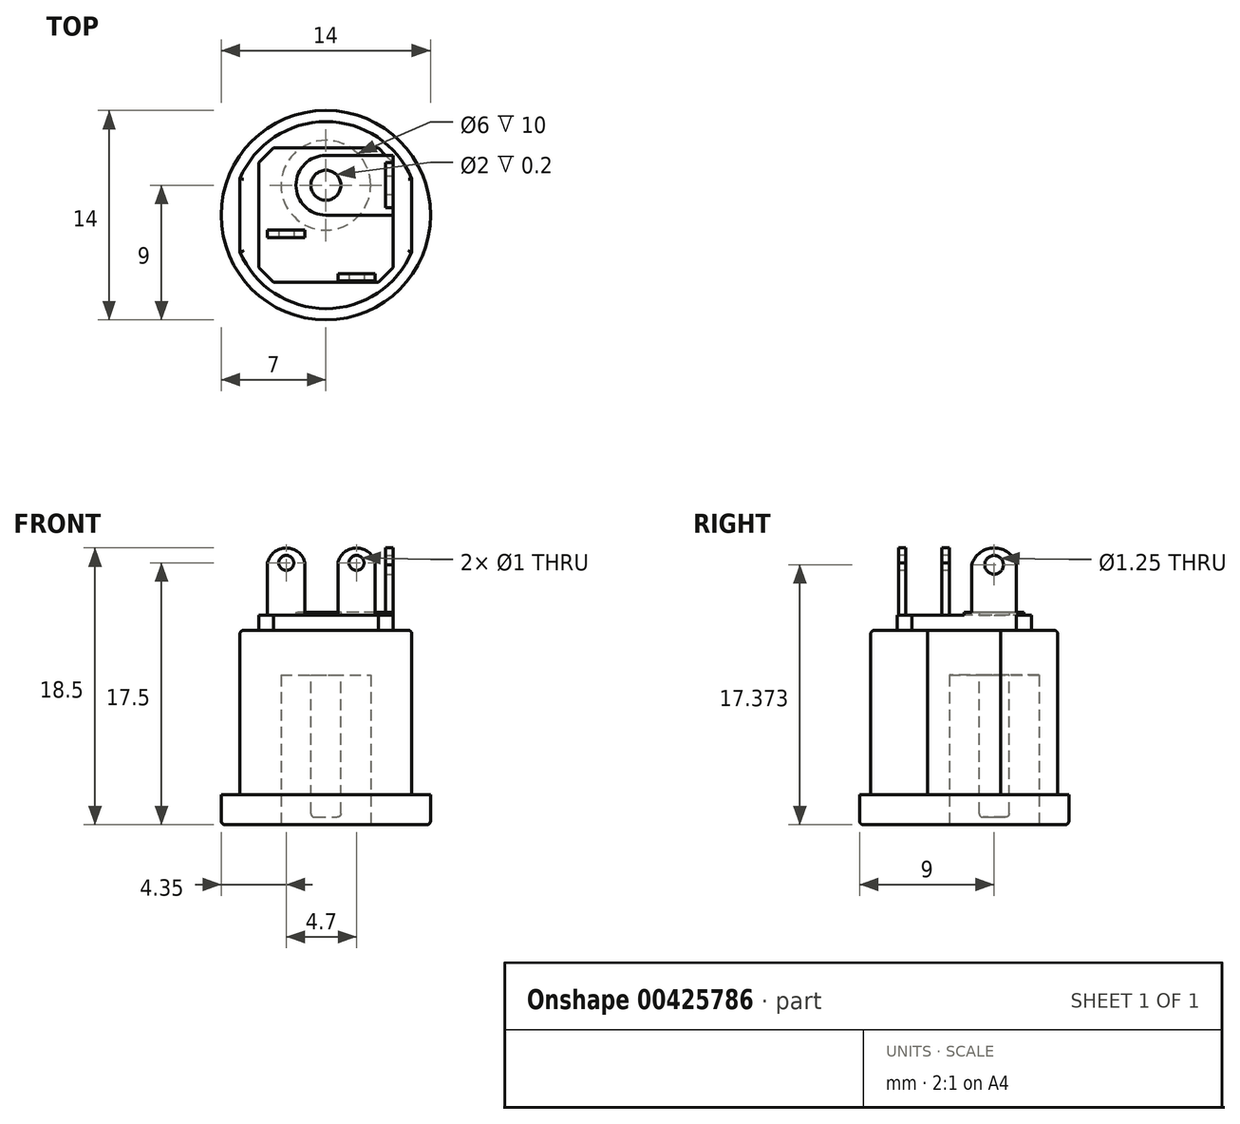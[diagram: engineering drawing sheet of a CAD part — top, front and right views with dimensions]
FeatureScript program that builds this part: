
annotation { "Feature Type Name" : "Feature", "Feature Type Description" : "" }
export const myFeature = defineFeature(function(context is Context, id is Id, definition is map)
    precondition{}
    {
        {
            var Q0;
            Q0=qCreatedBy(makeId("Top.planeOp"),FACE);
            var sketch = newSketch(context, id + "F0", { "sketchPlane" : qUnion([Q0])});
            skCircle(sketch, "E0", {"center": v(0, 0) * mm, "radius": 7 * mm});
            skSolve(sketch);
        }
        {
            var Q0;
            Q0 = qSketchRegion(id + "F0", true);
            extrude(context, id + "F1", {"entities" : qUnion([Q0]), "depth" : 2 * mm});
        }
        {
            var Q0;
            Q0=makeQuery(id+"F1.opExtrude","CAP_FACE",FACE,{"disambiguationData":[OSD([sQuery(id+"F0.wireOp",EDGE,"E0")])],"isStart":false});
            var sketch = newSketch(context, id + "F2", { "sketchPlane" : qUnion([Q0])});
            skArc(sketch, "E1", {"start": v(-5.75, -2.45) * mm, "mid": v(0, -6.25) * mm, "end": v(5.75, -2.45) * mm});
            skLineSegment(sketch, "E2", {"start": v(5.75, 2.45) * mm, "end": v(5.75, -2.45) * mm});
            skLineSegment(sketch, "E3", {"start": v(0, 8.24) * mm, "end": v(0, -10) * mm, "construction": true});
            skLineSegment(sketch, "E4.MirrorCS", {"start": v(-5.75, 2.45) * mm, "end": v(-5.75, -2.45) * mm});
            skPoint(sketch, "E5.orphan", {"position": v(-5.75, 5.82) * mm});
            skPoint(sketch, "E6.orphan", {"position": v(-5.75, -6.76) * mm});
            skPoint(sketch, "E7.orphan", {"position": v(5.75, 5.82) * mm});
            skArc(sketch, "E8.trimOffspring", {"start": v(5.75, 2.45) * mm, "mid": v(0, 6.25) * mm, "end": v(-5.75, 2.45) * mm});
            skPoint(sketch, "E9.orphan", {"position": v(5.75, -6.76) * mm});
            skSolve(sketch);
        }
        {
            var Q0;
            Q0 = qSketchRegion(id + "F2", true);
            extrude(context, id + "F3", {"entities" : qUnion([Q0]), "operationType" : NewBodyOperationType.ADD, "depth" : 11 * mm});
        }
        {
            var Q0;
            Q0=makeQuery(id+"F1.opExtrude","CAP_FACE",FACE,{"disambiguationData":[OSD([sQuery(id+"F0.wireOp",EDGE,"E0")])],"isStart":true});
            var sketch = newSketch(context, id + "F4", { "sketchPlane" : qUnion([Q0])});
            skCircle(sketch, "E10", {"center": v(0, -2) * mm, "radius": 3 * mm});
            skSolve(sketch);
        }
        {
            var Q0;
            Q0 = qSketchRegion(id + "F4", true);
            extrude(context, id + "F5", {"entities" : qUnion([Q0]), "operationType" : NewBodyOperationType.REMOVE, "oppositeDirection" : true, "depth" : 10 * mm});
        }
        {
            var Q0;
            Q0=makeQuery(id+"F3.opExtrude","CAP_FACE",FACE,{"disambiguationData":[OSD([sQuery(id+"F2.wireOp",EDGE,"E1"),sQuery(id+"F2.wireOp",EDGE,"E2"),sQuery(id+"F2.wireOp",EDGE,"E4.MirrorCS"),sQuery(id+"F2.wireOp",EDGE,"E8.trimOffspring")])],"isStart":false});
            var sketch = newSketch(context, id + "F6", { "sketchPlane" : qUnion([Q0])});
            skLineSegment(sketch, "E11.bottom", {"start": v(3.5, -4.5) * mm, "end": v(-3.5, -4.5) * mm});
            skLineSegment(sketch, "E11.top", {"start": v(3.5, 4.5) * mm, "end": v(-3.5, 4.5) * mm});
            skLineSegment(sketch, "E11.left", {"start": v(4.5, -3.5) * mm, "end": v(4.5, 3.5) * mm});
            skLineSegment(sketch, "E11.right", {"start": v(-4.5, -3.5) * mm, "end": v(-4.5, 3.5) * mm});
            skPoint(sketch, "E11.middle", {"position": v(0, 0) * mm});
            skLineSegment(sketch, "E12", {"start": v(3.5, 4.5) * mm, "end": v(4.5, 3.5) * mm});
            skLineSegment(sketch, "E13", {"start": v(-9.63, 0) * mm, "end": v(10.52, 0) * mm, "construction": true});
            skLineSegment(sketch, "E14", {"start": v(0, 8.25) * mm, "end": v(0, -8.62) * mm, "construction": true});
            skLineSegment(sketch, "E15.MirrorCS", {"start": v(-3.5, 4.5) * mm, "end": v(-4.5, 3.5) * mm});
            skLineSegment(sketch, "E16.MirrorCS", {"start": v(-3.5, -4.5) * mm, "end": v(-4.5, -3.5) * mm});
            skLineSegment(sketch, "E17.MirrorCS", {"start": v(3.5, -4.5) * mm, "end": v(4.5, -3.5) * mm});
            skPoint(sketch, "E18.orphan", {"position": v(-4.5, 4.5) * mm});
            skPoint(sketch, "E19.orphan", {"position": v(4.5, 4.5) * mm});
            skPoint(sketch, "E20.orphan", {"position": v(4.5, -4.5) * mm});
            skPoint(sketch, "E21.orphan", {"position": v(-4.5, -4.5) * mm});
            skSolve(sketch);
        }
        {
            var Q0;
            Q0 = qSketchRegion(id + "F6", true);
            extrude(context, id + "F7", {"entities" : qUnion([Q0]), "operationType" : NewBodyOperationType.ADD, "depth" : 1 * mm});
        }
        {
            var Q0;
            Q0=makeQuery(id+"F7.opExtrude","CAP_FACE",FACE,{"disambiguationData":[OSD([sQuery(id+"F6.wireOp",EDGE,"E11.bottom"),sQuery(id+"F6.wireOp",EDGE,"E11.top"),sQuery(id+"F6.wireOp",EDGE,"E11.left"),sQuery(id+"F6.wireOp",EDGE,"E11.right"),sQuery(id+"F6.wireOp",EDGE,"E12"),sQuery(id+"F6.wireOp",EDGE,"E15.MirrorCS"),sQuery(id+"F6.wireOp",EDGE,"E16.MirrorCS"),sQuery(id+"F6.wireOp",EDGE,"E17.MirrorCS")])],"isStart":false});
            var sketch = newSketch(context, id + "F8", { "sketchPlane" : qUnion([Q0])});
            skLineSegment(sketch, "E22.bottom", {"start": v(4.5, 4) * mm, "end": v(0, 4) * mm});
            skLineSegment(sketch, "E22.top", {"start": v(4.5, 0) * mm, "end": v(0, 0) * mm});
            skLineSegment(sketch, "E22.left", {"start": v(4.5, 4) * mm, "end": v(4.5, 0) * mm});
            skLineSegment(sketch, "E22.right", {"start": v(-2, 2) * mm, "end": v(-2, 2) * mm});
            skCircle(sketch, "E23", {"center": v(0, 2) * mm, "radius": 1 * mm});
            skPoint(sketch, "E24.visualSharp", {"position": v(-2, 4) * mm});
            skArc(sketch, "E24.filletArc", {"start": v(0, 4) * mm, "mid": v(-1.41, 3.41) * mm, "end": v(-2, 2) * mm});
            skPoint(sketch, "E25.visualSharp", {"position": v(-2, 0) * mm});
            skArc(sketch, "E25.filletArc", {"start": v(-2, 2) * mm, "mid": v(-1.41, 0.59) * mm, "end": v(0, 0) * mm});
            skSolve(sketch);
        }
        {
            var Q0;
            Q0 = qSketchRegion(id + "F8", true);
            extrude(context, id + "F9", {"entities" : qUnion([Q0]), "operationType" : NewBodyOperationType.ADD, "depth" : 0.2 * mm});
        }
        {
            var Q0;
            {var subQ0=sQuery(id+"F6.wireOp",EDGE,"E17.MirrorCS");var subQ1=sQuery(id+"F6.wireOp",EDGE,"E16.MirrorCS");var subQ2=sQuery(id+"F6.wireOp",EDGE,"E15.MirrorCS");var subQ8=sQuery(id+"F6.wireOp",EDGE,"E12");var subQ9=sQuery(id+"F6.wireOp",EDGE,"E11.bottom");var subQ10=sQuery(id+"F6.wireOp",EDGE,"E11.right");var subQ11=sQuery(id+"F6.wireOp",EDGE,"E11.top");var subQ12=sQuery(id+"F6.wireOp",EDGE,"E11.left");Q0=makeQuery(id+"F9.boolean.opBoolean","SPLIT",FACE,{"disambiguationData":[TD([makeQuery(id+"F7.opExtrude","SWEPT_FACE",FACE,{"disambiguationData":[OSD([subQ9])]})])],"derivedFrom":makeQuery(id+"F7.opExtrude","CAP_FACE",FACE,{"disambiguationData":[OSD([subQ9,subQ11,subQ12,subQ10,subQ8,subQ2,subQ1,subQ0])],"isStart":false})});}
            var sketch = newSketch(context, id + "F10", { "sketchPlane" : qUnion([Q0])});
            skLineSegment(sketch, "E26.bottom", {"start": v(4, 3.5) * mm, "end": v(4.5, 3.5) * mm});
            skLineSegment(sketch, "E26.top", {"start": v(4, 0.5) * mm, "end": v(4.5, 0.5) * mm});
            skLineSegment(sketch, "E26.left", {"start": v(4, 3.5) * mm, "end": v(4, 0.5) * mm});
            skLineSegment(sketch, "E26.right", {"start": v(4.5, 3.5) * mm, "end": v(4.5, 0.5) * mm});
            skLineSegment(sketch, "E27.bottom", {"start": v(0.8, -3.9) * mm, "end": v(3.3, -3.9) * mm});
            skLineSegment(sketch, "E27.top", {"start": v(0.8, -4.4) * mm, "end": v(3.3, -4.4) * mm});
            skLineSegment(sketch, "E27.left", {"start": v(0.8, -3.9) * mm, "end": v(0.8, -4.4) * mm});
            skLineSegment(sketch, "E27.right", {"start": v(3.3, -3.9) * mm, "end": v(3.3, -4.4) * mm});
            skLineSegment(sketch, "E28.bottom", {"start": v(-3.9, -1) * mm, "end": v(-1.4, -1) * mm});
            skLineSegment(sketch, "E28.top", {"start": v(-3.9, -1.5) * mm, "end": v(-1.4, -1.5) * mm});
            skLineSegment(sketch, "E28.left", {"start": v(-3.9, -1) * mm, "end": v(-3.9, -1.5) * mm});
            skLineSegment(sketch, "E28.right", {"start": v(-1.4, -1) * mm, "end": v(-1.4, -1.5) * mm});
            skSolve(sketch);
        }
        {
            var Q0;
            Q0 = qSketchRegion(id + "F10", true);
            extrude(context, id + "F11", {"entities" : qUnion([Q0]), "operationType" : NewBodyOperationType.ADD, "depth" : 4.5 * mm});
        }
        {
            var Q0;
            Q0=makeQuery(id+"F11.boolean.opBoolean","MERGE",FACE,{"derivedFrom":[makeQuery(id+"F9.boolean.opBoolean","MERGE",FACE,{"derivedFrom":[makeQuery(id+"F7.opExtrude","SWEPT_FACE",FACE,{"disambiguationData":[OSD([sQuery(id+"F6.wireOp",EDGE,"E11.left")])]}),makeQuery(id+"F9.opExtrude","SWEPT_FACE",FACE,{"disambiguationData":[OSD([sQuery(id+"F8.wireOp",EDGE,"E22.left")])]})]}),makeQuery(id+"F11.opExtrude","SWEPT_FACE",FACE,{"disambiguationData":[OSD([sQuery(id+"F10.wireOp",EDGE,"E26.right")])]})]});
            var sketch = newSketch(context, id + "F12", { "sketchPlane" : qUnion([Q0])});
            skCircle(sketch, "E29", {"center": v(2, 17.37) * mm, "radius": 0.62 * mm});
            skPoint(sketch, "E29.centerSnap0", {"position": v(2, 18.5) * mm});
            skArc(sketch, "E30", {"start": v(3.5, 17.37) * mm, "mid": v(2, 18.5) * mm, "end": v(0.5, 17.37) * mm});
            skSolve(sketch);
        }
        {
            var Q0;
            Q0 = qSketchRegion(id + "F12", true);
            var Q1;
            {var subQ0=sQuery(id+"F12.wireOp",EDGE,"E30");var subQ1=sQuery(id+"F10.wireOp",EDGE,"E26.right");var subQ4=makeQuery(id+"F11.opExtrude","CAP_EDGE",EDGE,{"disambiguationData":[OSD([subQ1])],"isStart":false});var subQ5=makeQuery(id+"F12.imprint","INTERSECT",VERTEX,{"derivedFrom":[subQ4,subQ0]});Q1=makeQuery(id+"F12.imprint","IMPRINT",FACE,{"disambiguationData":[TD([[makeQuery(id+"F12.imprint","IMPRINT",EDGE,{"disambiguationData":[TD([[subQ5,1.0]])],"derivedFrom":subQ0}),-1.0]])]});}
            var Q2;
            {var subQ0=sQuery(id+"F12.wireOp",EDGE,"E30");var subQ1=sQuery(id+"F10.wireOp",EDGE,"E26.right");var subQ4=makeQuery(id+"F11.opExtrude","CAP_EDGE",EDGE,{"disambiguationData":[OSD([subQ1])],"isStart":false});var subQ5=makeQuery(id+"F12.imprint","INTERSECT",VERTEX,{"derivedFrom":[subQ4,subQ0]});Q2=makeQuery(id+"F12.imprint","IMPRINT",FACE,{"disambiguationData":[TD([[makeQuery(id+"F12.imprint","IMPRINT",EDGE,{"disambiguationData":[TD([[subQ5,-1.0]])],"derivedFrom":subQ0}),-1.0]])]});}
            extrude(context, id + "F13", {"entities" : qUnion([Q0, Q1, Q2]), "operationType" : NewBodyOperationType.REMOVE, "oppositeDirection" : true, "depth" : 25 * mm});
        }
        {
            var Q0;
            Q0=makeQuery(id+"F11.opExtrude","SWEPT_FACE",FACE,{"disambiguationData":[OSD([sQuery(id+"F10.wireOp",EDGE,"E27.top")])]});
            var sketch = newSketch(context, id + "F14", { "sketchPlane" : qUnion([Q0])});
            skCircle(sketch, "E31", {"center": v(2.05, 17.5) * mm, "radius": 0.5 * mm});
            skPoint(sketch, "E31.centerSnap0", {"position": v(2.05, 18.5) * mm});
            skLineSegment(sketch, "E32.0.0", {"start": v(-3.9, 14) * mm, "end": v(-1.4, 14) * mm});
            skLineSegment(sketch, "E32.0.1", {"start": v(-1.4, 14) * mm, "end": v(-1.4, 18.5) * mm});
            skLineSegment(sketch, "E32.0.2", {"start": v(-1.4, 18.5) * mm, "end": v(-3.9, 18.5) * mm});
            skLineSegment(sketch, "E32.0.3", {"start": v(-3.9, 18.5) * mm, "end": v(-3.9, 14) * mm});
            skCircle(sketch, "E33", {"center": v(-2.65, 17.5) * mm, "radius": 0.5 * mm});
            skPoint(sketch, "E33.centerSnap0", {"position": v(-2.65, 18.5) * mm});
            skArc(sketch, "E34", {"start": v(-1.4, 17.5) * mm, "mid": v(-2.65, 18.5) * mm, "end": v(-3.9, 17.5) * mm});
            skArc(sketch, "E35", {"start": v(3.3, 17.5) * mm, "mid": v(2.05, 18.5) * mm, "end": v(0.8, 17.5) * mm});
            skSolve(sketch);
        }
        {
            var Q0;
            Q0=makeQuery(id+"F14.imprint","IMPRINT",FACE,{"disambiguationData":[TD([[makeQuery(id+"F14.imprint","IMPRINT",EDGE,{"derivedFrom":sQuery(id+"F14.wireOp",EDGE,"E31")}),1.0]])]});
            var Q1;
            {var subQ0=sQuery(id+"F14.wireOp",EDGE,"E35");var subQ1=sQuery(id+"F10.wireOp",EDGE,"E27.top");var subQ4=makeQuery(id+"F11.opExtrude","CAP_EDGE",EDGE,{"disambiguationData":[OSD([subQ1])],"isStart":false});var subQ5=makeQuery(id+"F14.imprint","INTERSECT",VERTEX,{"derivedFrom":[subQ4,subQ0]});Q1=makeQuery(id+"F14.imprint","IMPRINT",FACE,{"disambiguationData":[TD([[makeQuery(id+"F14.imprint","IMPRINT",EDGE,{"disambiguationData":[TD([[subQ5,-1.0]])],"derivedFrom":subQ0}),-1.0]])]});}
            var Q2;
            {var subQ0=sQuery(id+"F14.wireOp",EDGE,"E35");var subQ1=sQuery(id+"F10.wireOp",EDGE,"E27.top");var subQ4=makeQuery(id+"F11.opExtrude","CAP_EDGE",EDGE,{"disambiguationData":[OSD([subQ1])],"isStart":false});var subQ5=makeQuery(id+"F14.imprint","INTERSECT",VERTEX,{"derivedFrom":[subQ4,subQ0]});Q2=makeQuery(id+"F14.imprint","IMPRINT",FACE,{"disambiguationData":[TD([[makeQuery(id+"F14.imprint","IMPRINT",EDGE,{"disambiguationData":[TD([[subQ5,1.0]])],"derivedFrom":subQ0}),-1.0]])]});}
            var Q3;
            Q3=makeQuery(id+"F14.imprint","IMPRINT",FACE,{"disambiguationData":[TD([[makeQuery(id+"F14.imprint","IMPRINT",EDGE,{"derivedFrom":sQuery(id+"F14.wireOp",EDGE,"E33")}),1.0]])]});
            var Q4;
            {var subQ0=sQuery(id+"F14.wireOp",EDGE,"E32.0.3");var subQ1=sQuery(id+"F14.wireOp",EDGE,"E32.0.2");var subQ2=makeQuery(id+"F14.imprint","INTERSECT",VERTEX,{"derivedFrom":[subQ1,subQ0]});Q4=makeQuery(id+"F14.imprint","IMPRINT",FACE,{"disambiguationData":[TD([[makeQuery(id+"F14.imprint","IMPRINT",EDGE,{"disambiguationData":[TD([[subQ2,1.0]])],"derivedFrom":subQ1}),1.0]])]});}
            var Q5;
            {var subQ0=sQuery(id+"F14.wireOp",EDGE,"E32.0.2");var subQ1=sQuery(id+"F14.wireOp",EDGE,"E32.0.1");var subQ2=makeQuery(id+"F14.imprint","INTERSECT",VERTEX,{"derivedFrom":[subQ1,subQ0]});Q5=makeQuery(id+"F14.imprint","IMPRINT",FACE,{"disambiguationData":[TD([[makeQuery(id+"F14.imprint","IMPRINT",EDGE,{"disambiguationData":[TD([[subQ2,1.0]])],"derivedFrom":subQ1}),1.0]])]});}
            extrude(context, id + "F15", {"entities" : qUnion([Q0, Q1, Q2, Q3, Q4, Q5]), "operationType" : NewBodyOperationType.REMOVE, "endBound" : BoundingType.THROUGH_ALL, "oppositeDirection" : true, "depth" : 25 * mm});
        }
        {
            var Q0;
            Q0=makeQuery(id+"F5.boolean.opBoolean","COPY",FACE,{"derivedFrom":makeQuery(id+"F5.opExtrude","CAP_FACE",FACE,{"disambiguationData":[OSD([sQuery(id+"F4.wireOp",EDGE,"E10")])],"isStart":false})});
            var sketch = newSketch(context, id + "F16", { "sketchPlane" : qUnion([Q0])});
            skCircle(sketch, "E36.0", {"center": v(0, -2) * mm, "radius": 3 * mm, "construction": true});
            skCircle(sketch, "E37", {"center": v(0, -2) * mm, "radius": 1 * mm});
            skSolve(sketch);
        }
        {
            var Q0;
            Q0=makeQuery(id+"F16.imprint","IMPRINT",FACE,{"disambiguationData":[TD([[makeQuery(id+"F16.imprint","IMPRINT",EDGE,{"derivedFrom":sQuery(id+"F16.wireOp",EDGE,"E37")}),1.0]])]});
            extrude(context, id + "F17", {"entities" : qUnion([Q0]), "operationType" : NewBodyOperationType.ADD, "depth" : 9.5 * mm});
        }
        {
            var Q0;
            Q0=makeQuery(id+"F17.opExtrude","CAP_FACE",FACE,{"disambiguationData":[OSD([sQuery(id+"F16.wireOp",EDGE,"E37")])],"isStart":false});
            var Q1;
            Q1=makeQuery(id+"F1.opExtrude","CAP_EDGE",EDGE,{"disambiguationData":[OSD([sQuery(id+"F0.wireOp",EDGE,"E0")])],"isStart":true});
            var Q2;
            Q2=makeQuery(id+"F3.opExtrude","CAP_EDGE",EDGE,{"disambiguationData":[OSD([sQuery(id+"F2.wireOp",EDGE,"E8.trimOffspring")])],"isStart":false});
            var Q3;
            Q3=makeQuery(id+"F3.opExtrude","CAP_EDGE",EDGE,{"disambiguationData":[OSD([sQuery(id+"F2.wireOp",EDGE,"E2")])],"isStart":false});
            var Q4;
            Q4=makeQuery(id+"F3.opExtrude","CAP_EDGE",EDGE,{"disambiguationData":[OSD([sQuery(id+"F2.wireOp",EDGE,"E1")])],"isStart":false});
            var Q5;
            Q5=makeQuery(id+"F3.opExtrude","CAP_EDGE",EDGE,{"disambiguationData":[OSD([sQuery(id+"F2.wireOp",EDGE,"E4.MirrorCS")])],"isStart":false});
            fillet(context, id + "F18", {"entities" : qUnion([Q0, Q1, Q2, Q3, Q4, Q5]), "radius" : 0.25 * mm, "tangentPropagation" : true, "allowEdgeOverflow" : false});
        }
    });
